# Revit family: 94702-221
name_source: partatom
category: Equipamento especial
revit_build: Autodesk Revit 2016 (Build: 20150220_1215(x64)
units: mm (PartAtom-declared; Revit-internal decimal feet)

## family parameters
Com base no plano de trabalho = Não
Compartilhado = Não
Corte com vazios quando carregados = Não
Cota do conector redondo = Utilizar diâmetro
Ponto de cálculo do ambiente = Não
Sempre na vertical = Sim
Tipo de parte = Normal

## types (1)
- Tramontina - Cooktop a gás  Domino 2GG 30
    Classe de construção = classe II
    Consumo máximo = 4 kWh
    Código de montagem = 94702/201
    Descrição = Tramontina - Cooktop a gás - 94708/201
    Desenvolvedor = Factory Cursos & Desenvolvimento
    Eficiência energética = A
    Fabricante = Tramontina
    Frequência = 50 - 60 Hz
    Modelo = Tramontina - Dominó 2GG 30
    Nicho de instalação = 475 X 275  mm
    Peso Bruto = 6,1 kg
    Peso liquido = 5 kg
    Potência elétrica = 5 W
    Potência máxima - Auxiliar (1X) = 1,00kW
    Potência máxima - Rapido  (1X) = 3,0 kW
    Rendimento médio = 64%
    Site do desenvolvedor = www.factorycursos.com.br
    Tensão = 127 - 220 V
    Tramontina Referência = 94702/201
    URL = www.tramontina.com.br
